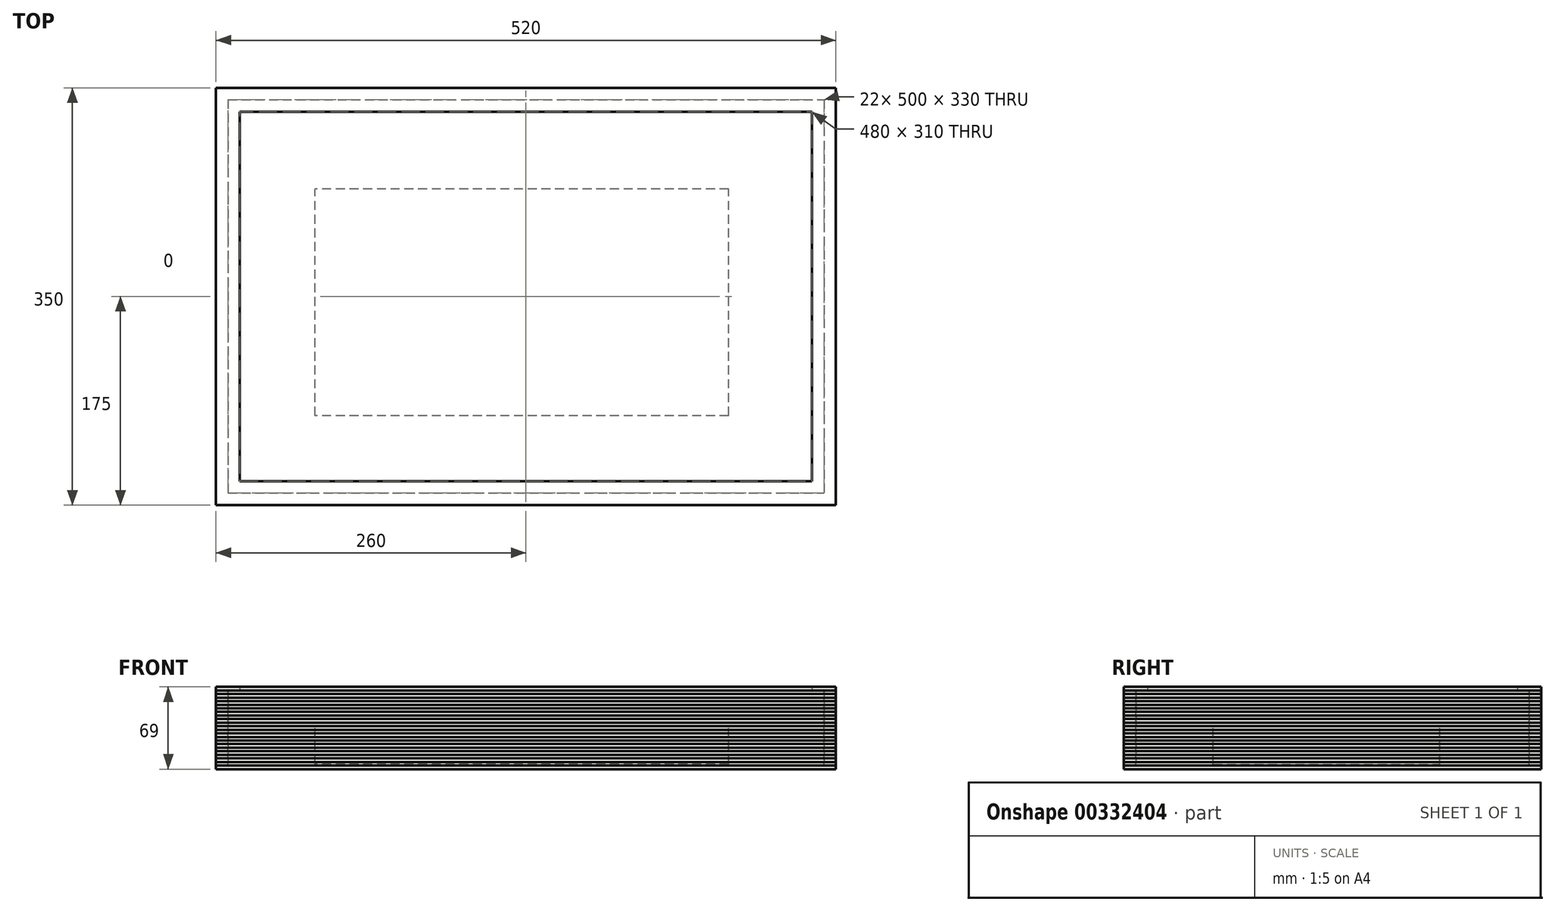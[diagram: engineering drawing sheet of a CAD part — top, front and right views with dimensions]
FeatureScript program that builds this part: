
annotation { "Feature Type Name" : "Feature", "Feature Type Description" : "" }
export const myFeature = defineFeature(function(context is Context, id is Id, definition is map)
    precondition{}
    {
        {
            var Q0;
            Q0=qCreatedBy(makeId("Top.planeOp"),FACE);
            var sketch = newSketch(context, id + "F0", { "sketchPlane" : qUnion([Q0])});
            skLineSegment(sketch, "E0.bottom", {"start": v(-250, 165) * mm, "end": v(250, 165) * mm});
            skLineSegment(sketch, "E0.top", {"start": v(-250, -165) * mm, "end": v(250, -165) * mm});
            skLineSegment(sketch, "E0.left", {"start": v(-250, 165) * mm, "end": v(-250, -165) * mm});
            skLineSegment(sketch, "E0.right", {"start": v(250, 165) * mm, "end": v(250, -165) * mm});
            skPoint(sketch, "E0.middle", {"position": v(0, 0) * mm});
            skSolve(sketch);
        }
        {
            var Q0;
            Q0=makeQuery(id+"F0.imprint","IMPRINT",FACE,{"disambiguationData":[TD([[makeQuery(id+"F0.imprint","IMPRINT",EDGE,{"derivedFrom":sQuery(id+"F0.wireOp",EDGE,"E0.bottom")}),-1.0]])]});
            var Q1;
            Q1 = qSketchRegion(id + "F6", true);
            extrude(context, id + "F1", {"entities" : qUnion([Q0, Q1]), "depth" : 27 * mm});
        }
        {
            var Q0;
            Q0=makeQuery(id+"F1.opExtrude","CAP_FACE",FACE,{"disambiguationData":[OSD([sQuery(id+"F0.wireOp",EDGE,"E0.bottom"),sQuery(id+"F0.wireOp",EDGE,"E0.top"),sQuery(id+"F0.wireOp",EDGE,"E0.left"),sQuery(id+"F0.wireOp",EDGE,"E0.right")])],"isStart":true});
            var sketch = newSketch(context, id + "F2", { "sketchPlane" : qUnion([Q0])});
            skLineSegment(sketch, "E1.bottom", {"start": v(170, 100) * mm, "end": v(-177, 100) * mm});
            skLineSegment(sketch, "E1.top", {"start": v(170, -90) * mm, "end": v(-177, -90) * mm});
            skLineSegment(sketch, "E1.left", {"start": v(170, 100) * mm, "end": v(170, -90) * mm});
            skLineSegment(sketch, "E1.right", {"start": v(-177, 100) * mm, "end": v(-177, -90) * mm});
            skSolve(sketch);
        }
        {
            var Q0;
            Q0=makeQuery(id+"F2.imprint","IMPRINT",FACE,{"disambiguationData":[TD([[makeQuery(id+"F2.imprint","IMPRINT",EDGE,{"derivedFrom":sQuery(id+"F2.wireOp",EDGE,"E1.bottom")}),1.0]])]});
            extrude(context, id + "F3", {"entities" : qUnion([Q0]), "operationType" : NewBodyOperationType.ADD, "depth" : 35 * mm});
        }
        {
            var Q0;
            Q0=makeQuery(id+"F1.opExtrude","CAP_FACE",FACE,{"disambiguationData":[OSD([sQuery(id+"F0.wireOp",EDGE,"E0.bottom"),sQuery(id+"F0.wireOp",EDGE,"E0.top"),sQuery(id+"F0.wireOp",EDGE,"E0.left"),sQuery(id+"F0.wireOp",EDGE,"E0.right")])],"isStart":false});
            var sketch = newSketch(context, id + "F4", { "sketchPlane" : qUnion([Q0])});
            skLineSegment(sketch, "E2.bottom", {"start": v(-260, 175) * mm, "end": v(260, 175) * mm});
            skLineSegment(sketch, "E2.top", {"start": v(-260, -175) * mm, "end": v(260, -175) * mm});
            skLineSegment(sketch, "E2.left", {"start": v(-260, 175) * mm, "end": v(-260, -175) * mm});
            skLineSegment(sketch, "E2.right", {"start": v(260, 175) * mm, "end": v(260, -175) * mm});
            skPoint(sketch, "E2.middle", {"position": v(0, 0) * mm});
            skLineSegment(sketch, "E3.bottom", {"start": v(240, 155) * mm, "end": v(-240, 155) * mm});
            skLineSegment(sketch, "E3.top", {"start": v(240, -155) * mm, "end": v(-240, -155) * mm});
            skLineSegment(sketch, "E3.left", {"start": v(240, 155) * mm, "end": v(240, -155) * mm});
            skLineSegment(sketch, "E3.right", {"start": v(-240, 155) * mm, "end": v(-240, -155) * mm});
            skSolve(sketch);
        }
        {
            var Q0;
            Q0=makeQuery(id+"F4.imprint","IMPRINT",FACE,{"disambiguationData":[TD([[makeQuery(id+"F4.imprint","IMPRINT",EDGE,{"derivedFrom":sQuery(id+"F4.wireOp",EDGE,"E3.bottom")}),-1.0]])]});
            var Q1;
            Q1=makeQuery(id+"F4.imprint","IMPRINT",FACE,{"disambiguationData":[TD([[makeQuery(id+"F4.imprint","IMPRINT",EDGE,{"derivedFrom":sQuery(id+"F4.wireOp",EDGE,"E2.bottom")}),-1.0]])]});
            extrude(context, id + "F5", {"entities" : qUnion([Q0, Q1]), "depth" : 3 * mm});
        }
        {
            var Q0;
            Q0=makeQuery(id+"F4.imprint","IMPRINT",FACE,{"disambiguationData":[TD([[makeQuery(id+"F4.imprint","IMPRINT",EDGE,{"derivedFrom":sQuery(id+"F4.wireOp",EDGE,"E2.bottom")}),-1.0]])]});
            var sketch = newSketch(context, id + "F6", { "sketchPlane" : qUnion([Q0])});
            skLineSegment(sketch, "E4.bottom", {"start": v(-260, -175) * mm, "end": v(260, -175) * mm});
            skLineSegment(sketch, "E4.top", {"start": v(-260, 175) * mm, "end": v(260, 175) * mm});
            skLineSegment(sketch, "E4.left", {"start": v(-260, -175) * mm, "end": v(-260, 175) * mm});
            skLineSegment(sketch, "E4.right", {"start": v(260, -175) * mm, "end": v(260, 175) * mm});
            skPoint(sketch, "E4.middle", {"position": v(0, 0) * mm});
            skLineSegment(sketch, "E5.bottom", {"start": v(-250, -165) * mm, "end": v(250, -165) * mm});
            skLineSegment(sketch, "E5.top", {"start": v(-250, 165) * mm, "end": v(250, 165) * mm});
            skLineSegment(sketch, "E5.left", {"start": v(-250, -165) * mm, "end": v(-250, 165) * mm});
            skLineSegment(sketch, "E5.right", {"start": v(250, -165) * mm, "end": v(250, 165) * mm});
            skSolve(sketch);
        }
        {
            var Q0;
            Q0=makeQuery(id+"F4.imprint","IMPRINT",FACE,{"disambiguationData":[TD([[makeQuery(id+"F4.imprint","IMPRINT",EDGE,{"derivedFrom":sQuery(id+"F4.wireOp",EDGE,"E2.bottom")}),-1.0]])]});
            var Q1;
            Q1 = qSketchRegion(id + "F6", true);
            extrude(context, id + "F7", {"entities" : qUnion([Q0, Q1]), "depth" : -3 * mm});
        }
        {
            var Q0;
            Q0=makeQuery(id+"F7.opExtrude","SWEPT_BODY",BODY,{"disambiguationData":[OSD([sQuery(id+"F6.wireOp",EDGE,"E4.bottom"),sQuery(id+"F6.wireOp",EDGE,"E4.top"),sQuery(id+"F6.wireOp",EDGE,"E4.left"),sQuery(id+"F6.wireOp",EDGE,"E4.right"),sQuery(id+"F6.wireOp",EDGE,"E5.bottom"),sQuery(id+"F6.wireOp",EDGE,"E5.top"),sQuery(id+"F6.wireOp",EDGE,"E5.left"),sQuery(id+"F6.wireOp",EDGE,"E5.right")])]});
            var Q1;
            Q1=makeQuery(id+"F7.opExtrude","CAP_FACE",FACE,{"disambiguationData":[OSD([sQuery(id+"F0.wireOp",EDGE,"E0.bottom"),sQuery(id+"F0.wireOp",EDGE,"E0.top"),sQuery(id+"F0.wireOp",EDGE,"E0.left"),sQuery(id+"F0.wireOp",EDGE,"E0.right"),sQuery(id+"F4.wireOp",EDGE,"E2.bottom"),sQuery(id+"F4.wireOp",EDGE,"E2.top"),sQuery(id+"F4.wireOp",EDGE,"E2.left"),sQuery(id+"F4.wireOp",EDGE,"E2.right")])],"isStart":false});
            mirror(context, id + "F8", {"entities" : qUnion([Q0]), "mirrorPlane" : qUnion([Q1])});
        }
        {
            var Q0;
            Q0=makeQuery(id+"F8.opPattern","COPY",BODY,{"derivedFrom":makeQuery(id+"F7.opExtrude","SWEPT_BODY",BODY,{"disambiguationData":[OSD([sQuery(id+"F6.wireOp",EDGE,"E4.bottom"),sQuery(id+"F6.wireOp",EDGE,"E4.top"),sQuery(id+"F6.wireOp",EDGE,"E4.left"),sQuery(id+"F6.wireOp",EDGE,"E4.right"),sQuery(id+"F6.wireOp",EDGE,"E5.bottom"),sQuery(id+"F6.wireOp",EDGE,"E5.top"),sQuery(id+"F6.wireOp",EDGE,"E5.left"),sQuery(id+"F6.wireOp",EDGE,"E5.right")])]}),"instanceName":"1"});
            var Q1;
            Q1=makeQuery(id+"F7.opExtrude","SWEPT_BODY",BODY,{"disambiguationData":[OSD([sQuery(id+"F0.wireOp",EDGE,"E0.bottom"),sQuery(id+"F0.wireOp",EDGE,"E0.top"),sQuery(id+"F0.wireOp",EDGE,"E0.left"),sQuery(id+"F0.wireOp",EDGE,"E0.right"),sQuery(id+"F4.wireOp",EDGE,"E2.bottom"),sQuery(id+"F4.wireOp",EDGE,"E2.top"),sQuery(id+"F4.wireOp",EDGE,"E2.left"),sQuery(id+"F4.wireOp",EDGE,"E2.right")])]});
            var Q2;
            Q2=makeQuery(id+"F8.opPattern","COPY",FACE,{"derivedFrom":makeQuery(id+"F7.opExtrude","CAP_FACE",FACE,{"disambiguationData":[OSD([sQuery(id+"F6.wireOp",EDGE,"E4.bottom"),sQuery(id+"F6.wireOp",EDGE,"E4.top"),sQuery(id+"F6.wireOp",EDGE,"E4.left"),sQuery(id+"F6.wireOp",EDGE,"E4.right"),sQuery(id+"F6.wireOp",EDGE,"E5.bottom"),sQuery(id+"F6.wireOp",EDGE,"E5.top"),sQuery(id+"F6.wireOp",EDGE,"E5.left"),sQuery(id+"F6.wireOp",EDGE,"E5.right")])],"isStart":true}),"instanceName":"1"});
            mirror(context, id + "F9", {"entities" : qUnion([Q0, Q1]), "mirrorPlane" : qUnion([Q2])});
        }
        {
            var Q0;
            Q0=makeQuery(id+"F9.opPattern","COPY",BODY,{"derivedFrom":makeQuery(id+"F7.opExtrude","SWEPT_BODY",BODY,{"disambiguationData":[OSD([sQuery(id+"F0.wireOp",EDGE,"E0.bottom"),sQuery(id+"F0.wireOp",EDGE,"E0.top"),sQuery(id+"F0.wireOp",EDGE,"E0.left"),sQuery(id+"F0.wireOp",EDGE,"E0.right"),sQuery(id+"F4.wireOp",EDGE,"E2.bottom"),sQuery(id+"F4.wireOp",EDGE,"E2.top"),sQuery(id+"F4.wireOp",EDGE,"E2.left"),sQuery(id+"F4.wireOp",EDGE,"E2.right")])]}),"instanceName":"1"});
            var Q1;
            Q1=makeQuery(id+"F9.opPattern","COPY",BODY,{"derivedFrom":makeQuery(id+"F8.opPattern","COPY",BODY,{"derivedFrom":makeQuery(id+"F7.opExtrude","SWEPT_BODY",BODY,{"disambiguationData":[OSD([sQuery(id+"F6.wireOp",EDGE,"E4.bottom"),sQuery(id+"F6.wireOp",EDGE,"E4.top"),sQuery(id+"F6.wireOp",EDGE,"E4.left"),sQuery(id+"F6.wireOp",EDGE,"E4.right"),sQuery(id+"F6.wireOp",EDGE,"E5.bottom"),sQuery(id+"F6.wireOp",EDGE,"E5.top"),sQuery(id+"F6.wireOp",EDGE,"E5.left"),sQuery(id+"F6.wireOp",EDGE,"E5.right")])]}),"instanceName":"1"}),"instanceName":"1"});
            var Q2;
            Q2=makeQuery(id+"F8.opPattern","COPY",BODY,{"derivedFrom":makeQuery(id+"F7.opExtrude","SWEPT_BODY",BODY,{"disambiguationData":[OSD([sQuery(id+"F6.wireOp",EDGE,"E4.bottom"),sQuery(id+"F6.wireOp",EDGE,"E4.top"),sQuery(id+"F6.wireOp",EDGE,"E4.left"),sQuery(id+"F6.wireOp",EDGE,"E4.right"),sQuery(id+"F6.wireOp",EDGE,"E5.bottom"),sQuery(id+"F6.wireOp",EDGE,"E5.top"),sQuery(id+"F6.wireOp",EDGE,"E5.left"),sQuery(id+"F6.wireOp",EDGE,"E5.right")])]}),"instanceName":"1"});
            var Q3;
            Q3=makeQuery(id+"F7.opExtrude","SWEPT_BODY",BODY,{"disambiguationData":[OSD([sQuery(id+"F0.wireOp",EDGE,"E0.bottom"),sQuery(id+"F0.wireOp",EDGE,"E0.top"),sQuery(id+"F0.wireOp",EDGE,"E0.left"),sQuery(id+"F0.wireOp",EDGE,"E0.right"),sQuery(id+"F4.wireOp",EDGE,"E2.bottom"),sQuery(id+"F4.wireOp",EDGE,"E2.top"),sQuery(id+"F4.wireOp",EDGE,"E2.left"),sQuery(id+"F4.wireOp",EDGE,"E2.right")])]});
            var Q4;
            Q4=makeQuery(id+"F9.opPattern","COPY",FACE,{"derivedFrom":makeQuery(id+"F7.opExtrude","CAP_FACE",FACE,{"disambiguationData":[OSD([sQuery(id+"F0.wireOp",EDGE,"E0.bottom"),sQuery(id+"F0.wireOp",EDGE,"E0.top"),sQuery(id+"F0.wireOp",EDGE,"E0.left"),sQuery(id+"F0.wireOp",EDGE,"E0.right"),sQuery(id+"F4.wireOp",EDGE,"E2.bottom"),sQuery(id+"F4.wireOp",EDGE,"E2.top"),sQuery(id+"F4.wireOp",EDGE,"E2.left"),sQuery(id+"F4.wireOp",EDGE,"E2.right")])],"isStart":true}),"instanceName":"1"});
            mirror(context, id + "F10", {"entities" : qUnion([Q0, Q1, Q2, Q3]), "mirrorPlane" : qUnion([Q4])});
        }
        {
            var Q0;
            Q0=makeQuery(id+"F10.opPattern","COPY",BODY,{"derivedFrom":makeQuery(id+"F7.opExtrude","SWEPT_BODY",BODY,{"disambiguationData":[OSD([sQuery(id+"F0.wireOp",EDGE,"E0.bottom"),sQuery(id+"F0.wireOp",EDGE,"E0.top"),sQuery(id+"F0.wireOp",EDGE,"E0.left"),sQuery(id+"F0.wireOp",EDGE,"E0.right"),sQuery(id+"F4.wireOp",EDGE,"E2.bottom"),sQuery(id+"F4.wireOp",EDGE,"E2.top"),sQuery(id+"F4.wireOp",EDGE,"E2.left"),sQuery(id+"F4.wireOp",EDGE,"E2.right")])]}),"instanceName":"1"});
            var Q1;
            Q1=makeQuery(id+"F10.opPattern","COPY",BODY,{"derivedFrom":makeQuery(id+"F8.opPattern","COPY",BODY,{"derivedFrom":makeQuery(id+"F7.opExtrude","SWEPT_BODY",BODY,{"disambiguationData":[OSD([sQuery(id+"F6.wireOp",EDGE,"E4.bottom"),sQuery(id+"F6.wireOp",EDGE,"E4.top"),sQuery(id+"F6.wireOp",EDGE,"E4.left"),sQuery(id+"F6.wireOp",EDGE,"E4.right"),sQuery(id+"F6.wireOp",EDGE,"E5.bottom"),sQuery(id+"F6.wireOp",EDGE,"E5.top"),sQuery(id+"F6.wireOp",EDGE,"E5.left"),sQuery(id+"F6.wireOp",EDGE,"E5.right")])]}),"instanceName":"1"}),"instanceName":"1"});
            var Q2;
            Q2=makeQuery(id+"F10.opPattern","COPY",BODY,{"derivedFrom":makeQuery(id+"F9.opPattern","COPY",BODY,{"derivedFrom":makeQuery(id+"F8.opPattern","COPY",BODY,{"derivedFrom":makeQuery(id+"F7.opExtrude","SWEPT_BODY",BODY,{"disambiguationData":[OSD([sQuery(id+"F6.wireOp",EDGE,"E4.bottom"),sQuery(id+"F6.wireOp",EDGE,"E4.top"),sQuery(id+"F6.wireOp",EDGE,"E4.left"),sQuery(id+"F6.wireOp",EDGE,"E4.right"),sQuery(id+"F6.wireOp",EDGE,"E5.bottom"),sQuery(id+"F6.wireOp",EDGE,"E5.top"),sQuery(id+"F6.wireOp",EDGE,"E5.left"),sQuery(id+"F6.wireOp",EDGE,"E5.right")])]}),"instanceName":"1"}),"instanceName":"1"}),"instanceName":"1"});
            var Q3;
            Q3=makeQuery(id+"F10.opPattern","COPY",BODY,{"derivedFrom":makeQuery(id+"F9.opPattern","COPY",BODY,{"derivedFrom":makeQuery(id+"F7.opExtrude","SWEPT_BODY",BODY,{"disambiguationData":[OSD([sQuery(id+"F0.wireOp",EDGE,"E0.bottom"),sQuery(id+"F0.wireOp",EDGE,"E0.top"),sQuery(id+"F0.wireOp",EDGE,"E0.left"),sQuery(id+"F0.wireOp",EDGE,"E0.right"),sQuery(id+"F4.wireOp",EDGE,"E2.bottom"),sQuery(id+"F4.wireOp",EDGE,"E2.top"),sQuery(id+"F4.wireOp",EDGE,"E2.left"),sQuery(id+"F4.wireOp",EDGE,"E2.right")])]}),"instanceName":"1"}),"instanceName":"1"});
            var Q4;
            Q4=makeQuery(id+"F9.opPattern","COPY",BODY,{"derivedFrom":makeQuery(id+"F7.opExtrude","SWEPT_BODY",BODY,{"disambiguationData":[OSD([sQuery(id+"F0.wireOp",EDGE,"E0.bottom"),sQuery(id+"F0.wireOp",EDGE,"E0.top"),sQuery(id+"F0.wireOp",EDGE,"E0.left"),sQuery(id+"F0.wireOp",EDGE,"E0.right"),sQuery(id+"F4.wireOp",EDGE,"E2.bottom"),sQuery(id+"F4.wireOp",EDGE,"E2.top"),sQuery(id+"F4.wireOp",EDGE,"E2.left"),sQuery(id+"F4.wireOp",EDGE,"E2.right")])]}),"instanceName":"1"});
            var Q5;
            Q5=makeQuery(id+"F9.opPattern","COPY",BODY,{"derivedFrom":makeQuery(id+"F8.opPattern","COPY",BODY,{"derivedFrom":makeQuery(id+"F7.opExtrude","SWEPT_BODY",BODY,{"disambiguationData":[OSD([sQuery(id+"F6.wireOp",EDGE,"E4.bottom"),sQuery(id+"F6.wireOp",EDGE,"E4.top"),sQuery(id+"F6.wireOp",EDGE,"E4.left"),sQuery(id+"F6.wireOp",EDGE,"E4.right"),sQuery(id+"F6.wireOp",EDGE,"E5.bottom"),sQuery(id+"F6.wireOp",EDGE,"E5.top"),sQuery(id+"F6.wireOp",EDGE,"E5.left"),sQuery(id+"F6.wireOp",EDGE,"E5.right")])]}),"instanceName":"1"}),"instanceName":"1"});
            var Q6;
            Q6=makeQuery(id+"F8.opPattern","COPY",BODY,{"derivedFrom":makeQuery(id+"F7.opExtrude","SWEPT_BODY",BODY,{"disambiguationData":[OSD([sQuery(id+"F6.wireOp",EDGE,"E4.bottom"),sQuery(id+"F6.wireOp",EDGE,"E4.top"),sQuery(id+"F6.wireOp",EDGE,"E4.left"),sQuery(id+"F6.wireOp",EDGE,"E4.right"),sQuery(id+"F6.wireOp",EDGE,"E5.bottom"),sQuery(id+"F6.wireOp",EDGE,"E5.top"),sQuery(id+"F6.wireOp",EDGE,"E5.left"),sQuery(id+"F6.wireOp",EDGE,"E5.right")])]}),"instanceName":"1"});
            var Q7;
            Q7=makeQuery(id+"F7.opExtrude","SWEPT_BODY",BODY,{"disambiguationData":[OSD([sQuery(id+"F0.wireOp",EDGE,"E0.bottom"),sQuery(id+"F0.wireOp",EDGE,"E0.top"),sQuery(id+"F0.wireOp",EDGE,"E0.left"),sQuery(id+"F0.wireOp",EDGE,"E0.right"),sQuery(id+"F4.wireOp",EDGE,"E2.bottom"),sQuery(id+"F4.wireOp",EDGE,"E2.top"),sQuery(id+"F4.wireOp",EDGE,"E2.left"),sQuery(id+"F4.wireOp",EDGE,"E2.right")])]});
            var Q8;
            Q8=makeQuery(id+"F10.opPattern","COPY",FACE,{"derivedFrom":makeQuery(id+"F7.opExtrude","CAP_FACE",FACE,{"disambiguationData":[OSD([sQuery(id+"F0.wireOp",EDGE,"E0.bottom"),sQuery(id+"F0.wireOp",EDGE,"E0.top"),sQuery(id+"F0.wireOp",EDGE,"E0.left"),sQuery(id+"F0.wireOp",EDGE,"E0.right"),sQuery(id+"F4.wireOp",EDGE,"E2.bottom"),sQuery(id+"F4.wireOp",EDGE,"E2.top"),sQuery(id+"F4.wireOp",EDGE,"E2.left"),sQuery(id+"F4.wireOp",EDGE,"E2.right")])],"isStart":true}),"instanceName":"1"});
            mirror(context, id + "F11", {"entities" : qUnion([Q0, Q1, Q2, Q3, Q4, Q5, Q6, Q7]), "mirrorPlane" : qUnion([Q8])});
        }
        {
            var Q0;
            Q0=makeQuery(id+"F11.opPattern","COPY",BODY,{"derivedFrom":makeQuery(id+"F7.opExtrude","SWEPT_BODY",BODY,{"disambiguationData":[OSD([sQuery(id+"F0.wireOp",EDGE,"E0.bottom"),sQuery(id+"F0.wireOp",EDGE,"E0.top"),sQuery(id+"F0.wireOp",EDGE,"E0.left"),sQuery(id+"F0.wireOp",EDGE,"E0.right"),sQuery(id+"F4.wireOp",EDGE,"E2.bottom"),sQuery(id+"F4.wireOp",EDGE,"E2.top"),sQuery(id+"F4.wireOp",EDGE,"E2.left"),sQuery(id+"F4.wireOp",EDGE,"E2.right")])]}),"instanceName":"1"});
            var Q1;
            Q1=makeQuery(id+"F11.opPattern","COPY",BODY,{"derivedFrom":makeQuery(id+"F8.opPattern","COPY",BODY,{"derivedFrom":makeQuery(id+"F7.opExtrude","SWEPT_BODY",BODY,{"disambiguationData":[OSD([sQuery(id+"F6.wireOp",EDGE,"E4.bottom"),sQuery(id+"F6.wireOp",EDGE,"E4.top"),sQuery(id+"F6.wireOp",EDGE,"E4.left"),sQuery(id+"F6.wireOp",EDGE,"E4.right"),sQuery(id+"F6.wireOp",EDGE,"E5.bottom"),sQuery(id+"F6.wireOp",EDGE,"E5.top"),sQuery(id+"F6.wireOp",EDGE,"E5.left"),sQuery(id+"F6.wireOp",EDGE,"E5.right")])]}),"instanceName":"1"}),"instanceName":"1"});
            var Q2;
            Q2=makeQuery(id+"F11.opPattern","COPY",BODY,{"derivedFrom":makeQuery(id+"F9.opPattern","COPY",BODY,{"derivedFrom":makeQuery(id+"F8.opPattern","COPY",BODY,{"derivedFrom":makeQuery(id+"F7.opExtrude","SWEPT_BODY",BODY,{"disambiguationData":[OSD([sQuery(id+"F6.wireOp",EDGE,"E4.bottom"),sQuery(id+"F6.wireOp",EDGE,"E4.top"),sQuery(id+"F6.wireOp",EDGE,"E4.left"),sQuery(id+"F6.wireOp",EDGE,"E4.right"),sQuery(id+"F6.wireOp",EDGE,"E5.bottom"),sQuery(id+"F6.wireOp",EDGE,"E5.top"),sQuery(id+"F6.wireOp",EDGE,"E5.left"),sQuery(id+"F6.wireOp",EDGE,"E5.right")])]}),"instanceName":"1"}),"instanceName":"1"}),"instanceName":"1"});
            var Q3;
            Q3=makeQuery(id+"F11.opPattern","COPY",BODY,{"derivedFrom":makeQuery(id+"F9.opPattern","COPY",BODY,{"derivedFrom":makeQuery(id+"F7.opExtrude","SWEPT_BODY",BODY,{"disambiguationData":[OSD([sQuery(id+"F0.wireOp",EDGE,"E0.bottom"),sQuery(id+"F0.wireOp",EDGE,"E0.top"),sQuery(id+"F0.wireOp",EDGE,"E0.left"),sQuery(id+"F0.wireOp",EDGE,"E0.right"),sQuery(id+"F4.wireOp",EDGE,"E2.bottom"),sQuery(id+"F4.wireOp",EDGE,"E2.top"),sQuery(id+"F4.wireOp",EDGE,"E2.left"),sQuery(id+"F4.wireOp",EDGE,"E2.right")])]}),"instanceName":"1"}),"instanceName":"1"});
            var Q4;
            Q4=makeQuery(id+"F11.opPattern","COPY",BODY,{"derivedFrom":makeQuery(id+"F10.opPattern","COPY",BODY,{"derivedFrom":makeQuery(id+"F9.opPattern","COPY",BODY,{"derivedFrom":makeQuery(id+"F7.opExtrude","SWEPT_BODY",BODY,{"disambiguationData":[OSD([sQuery(id+"F0.wireOp",EDGE,"E0.bottom"),sQuery(id+"F0.wireOp",EDGE,"E0.top"),sQuery(id+"F0.wireOp",EDGE,"E0.left"),sQuery(id+"F0.wireOp",EDGE,"E0.right"),sQuery(id+"F4.wireOp",EDGE,"E2.bottom"),sQuery(id+"F4.wireOp",EDGE,"E2.top"),sQuery(id+"F4.wireOp",EDGE,"E2.left"),sQuery(id+"F4.wireOp",EDGE,"E2.right")])]}),"instanceName":"1"}),"instanceName":"1"}),"instanceName":"1"});
            var Q5;
            Q5=makeQuery(id+"F11.opPattern","COPY",BODY,{"derivedFrom":makeQuery(id+"F10.opPattern","COPY",BODY,{"derivedFrom":makeQuery(id+"F9.opPattern","COPY",BODY,{"derivedFrom":makeQuery(id+"F8.opPattern","COPY",BODY,{"derivedFrom":makeQuery(id+"F7.opExtrude","SWEPT_BODY",BODY,{"disambiguationData":[OSD([sQuery(id+"F6.wireOp",EDGE,"E4.bottom"),sQuery(id+"F6.wireOp",EDGE,"E4.top"),sQuery(id+"F6.wireOp",EDGE,"E4.left"),sQuery(id+"F6.wireOp",EDGE,"E4.right"),sQuery(id+"F6.wireOp",EDGE,"E5.bottom"),sQuery(id+"F6.wireOp",EDGE,"E5.top"),sQuery(id+"F6.wireOp",EDGE,"E5.left"),sQuery(id+"F6.wireOp",EDGE,"E5.right")])]}),"instanceName":"1"}),"instanceName":"1"}),"instanceName":"1"}),"instanceName":"1"});
            var Q6;
            Q6=makeQuery(id+"F11.opPattern","COPY",BODY,{"derivedFrom":makeQuery(id+"F10.opPattern","COPY",BODY,{"derivedFrom":makeQuery(id+"F7.opExtrude","SWEPT_BODY",BODY,{"disambiguationData":[OSD([sQuery(id+"F0.wireOp",EDGE,"E0.bottom"),sQuery(id+"F0.wireOp",EDGE,"E0.top"),sQuery(id+"F0.wireOp",EDGE,"E0.left"),sQuery(id+"F0.wireOp",EDGE,"E0.right"),sQuery(id+"F4.wireOp",EDGE,"E2.bottom"),sQuery(id+"F4.wireOp",EDGE,"E2.top"),sQuery(id+"F4.wireOp",EDGE,"E2.left"),sQuery(id+"F4.wireOp",EDGE,"E2.right")])]}),"instanceName":"1"}),"instanceName":"1"});
            var Q7;
            Q7=makeQuery(id+"F11.opPattern","COPY",FACE,{"derivedFrom":makeQuery(id+"F7.opExtrude","CAP_FACE",FACE,{"disambiguationData":[OSD([sQuery(id+"F0.wireOp",EDGE,"E0.bottom"),sQuery(id+"F0.wireOp",EDGE,"E0.top"),sQuery(id+"F0.wireOp",EDGE,"E0.left"),sQuery(id+"F0.wireOp",EDGE,"E0.right"),sQuery(id+"F4.wireOp",EDGE,"E2.bottom"),sQuery(id+"F4.wireOp",EDGE,"E2.top"),sQuery(id+"F4.wireOp",EDGE,"E2.left"),sQuery(id+"F4.wireOp",EDGE,"E2.right")])],"isStart":true}),"instanceName":"1"});
            mirror(context, id + "F12", {"entities" : qUnion([Q0, Q1, Q2, Q3, Q4, Q5, Q6]), "mirrorPlane" : qUnion([Q7])});
        }
        {
            var Q0;
            Q0=makeQuery(id+"F12.opPattern","COPY",BODY,{"derivedFrom":makeQuery(id+"F11.opPattern","COPY",BODY,{"derivedFrom":makeQuery(id+"F10.opPattern","COPY",BODY,{"derivedFrom":makeQuery(id+"F7.opExtrude","SWEPT_BODY",BODY,{"disambiguationData":[OSD([sQuery(id+"F0.wireOp",EDGE,"E0.bottom"),sQuery(id+"F0.wireOp",EDGE,"E0.top"),sQuery(id+"F0.wireOp",EDGE,"E0.left"),sQuery(id+"F0.wireOp",EDGE,"E0.right"),sQuery(id+"F4.wireOp",EDGE,"E2.bottom"),sQuery(id+"F4.wireOp",EDGE,"E2.top"),sQuery(id+"F4.wireOp",EDGE,"E2.left"),sQuery(id+"F4.wireOp",EDGE,"E2.right")])]}),"instanceName":"1"}),"instanceName":"1"}),"instanceName":"1"});
            deleteBodies(context, id + "F13", {"entities" : qUnion([Q0])});
        }
        {
            var Q0;
            Q0=makeQuery(id+"F12.opPattern","COPY",BODY,{"derivedFrom":makeQuery(id+"F11.opPattern","COPY",BODY,{"derivedFrom":makeQuery(id+"F10.opPattern","COPY",BODY,{"derivedFrom":makeQuery(id+"F9.opPattern","COPY",BODY,{"derivedFrom":makeQuery(id+"F8.opPattern","COPY",BODY,{"derivedFrom":makeQuery(id+"F7.opExtrude","SWEPT_BODY",BODY,{"disambiguationData":[OSD([sQuery(id+"F6.wireOp",EDGE,"E4.bottom"),sQuery(id+"F6.wireOp",EDGE,"E4.top"),sQuery(id+"F6.wireOp",EDGE,"E4.left"),sQuery(id+"F6.wireOp",EDGE,"E4.right"),sQuery(id+"F6.wireOp",EDGE,"E5.bottom"),sQuery(id+"F6.wireOp",EDGE,"E5.top"),sQuery(id+"F6.wireOp",EDGE,"E5.left"),sQuery(id+"F6.wireOp",EDGE,"E5.right")])]}),"instanceName":"1"}),"instanceName":"1"}),"instanceName":"1"}),"instanceName":"1"}),"instanceName":"1"});
            deleteBodies(context, id + "F14", {"entities" : qUnion([Q0])});
        }
        {
            var Q0;
            Q0=makeQuery(id+"F12.opPattern","COPY",FACE,{"derivedFrom":makeQuery(id+"F11.opPattern","COPY",FACE,{"derivedFrom":makeQuery(id+"F10.opPattern","COPY",FACE,{"derivedFrom":makeQuery(id+"F9.opPattern","COPY",FACE,{"derivedFrom":makeQuery(id+"F7.opExtrude","CAP_FACE",FACE,{"disambiguationData":[OSD([sQuery(id+"F0.wireOp",EDGE,"E0.bottom"),sQuery(id+"F0.wireOp",EDGE,"E0.top"),sQuery(id+"F0.wireOp",EDGE,"E0.left"),sQuery(id+"F0.wireOp",EDGE,"E0.right"),sQuery(id+"F4.wireOp",EDGE,"E2.bottom"),sQuery(id+"F4.wireOp",EDGE,"E2.top"),sQuery(id+"F4.wireOp",EDGE,"E2.left"),sQuery(id+"F4.wireOp",EDGE,"E2.right")])],"isStart":false}),"instanceName":"1"}),"instanceName":"1"}),"instanceName":"1"}),"instanceName":"1"});
            var sketch = newSketch(context, id + "F15", { "sketchPlane" : qUnion([Q0])});
            skLineSegment(sketch, "E6.bottom", {"start": v(260, 175) * mm, "end": v(-260, 175) * mm});
            skLineSegment(sketch, "E6.top", {"start": v(260, -175) * mm, "end": v(-260, -175) * mm});
            skLineSegment(sketch, "E6.left", {"start": v(260, 175) * mm, "end": v(260, -175) * mm});
            skLineSegment(sketch, "E6.right", {"start": v(-260, 175) * mm, "end": v(-260, -175) * mm});
            skPoint(sketch, "E6.middle", {"position": v(0, 0) * mm});
            skSolve(sketch);
        }
        {
            var Q0;
            Q0 = qSketchRegion(id + "F15", true);
            extrude(context, id + "F16", {"entities" : qUnion([Q0]), "depth" : 3 * mm});
        }
    });
